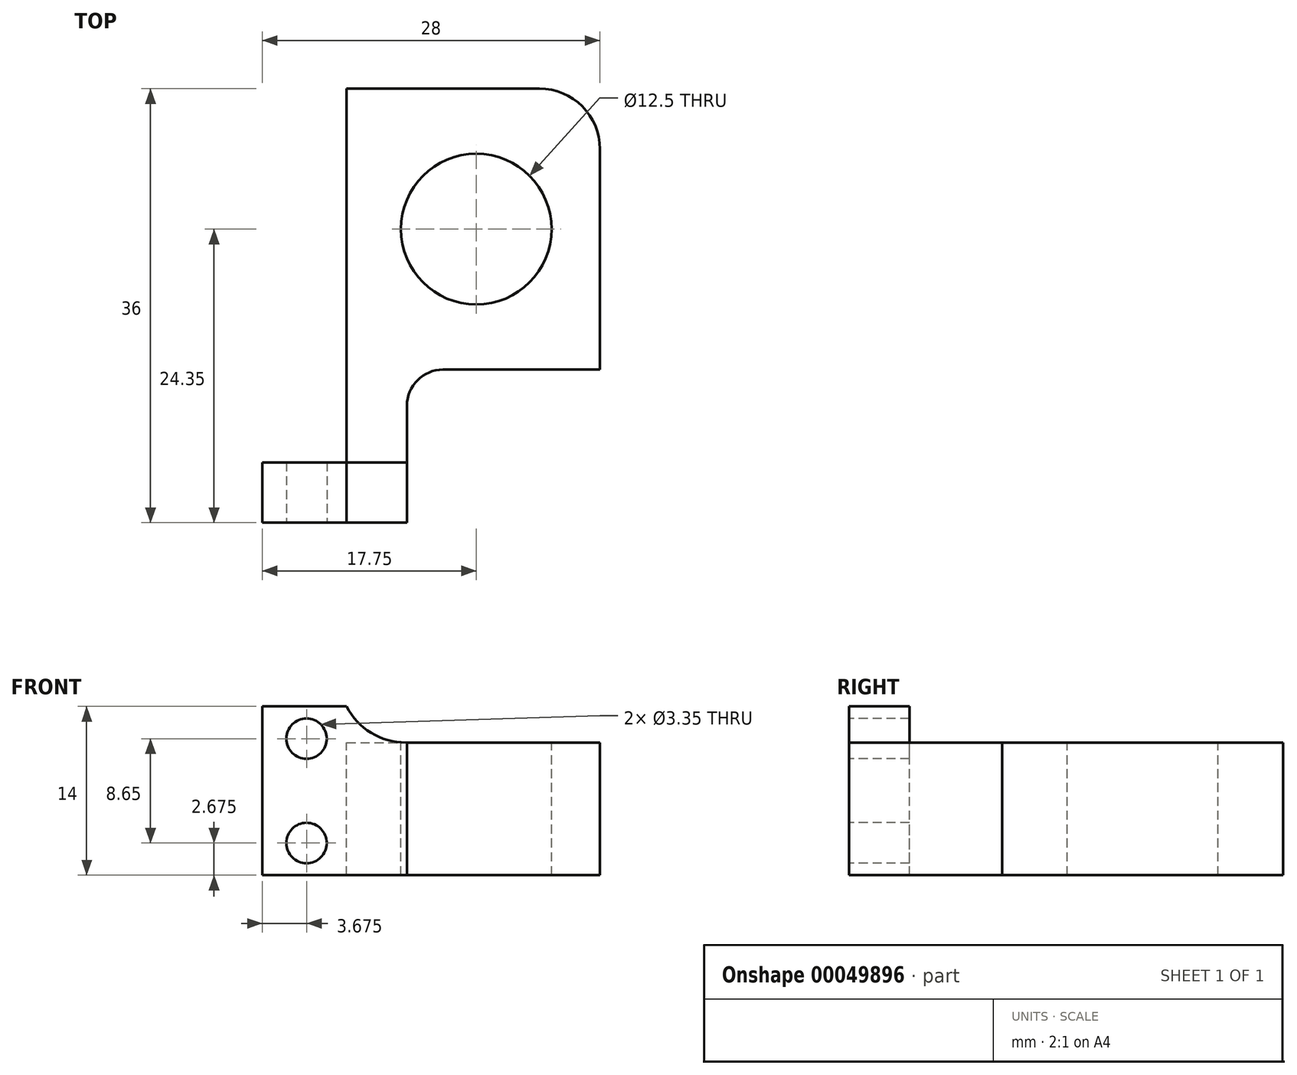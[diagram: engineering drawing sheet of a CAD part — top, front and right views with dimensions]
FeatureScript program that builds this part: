
annotation { "Feature Type Name" : "Feature", "Feature Type Description" : "" }
export const myFeature = defineFeature(function(context is Context, id is Id, definition is map)
    precondition{}
    {
        {
            var Q0;
            Q0=qCreatedBy(makeId("Top.planeOp"),FACE);
            var sketch = newSketch(context, id + "F0", { "sketchPlane" : qUnion([Q0])});
            skLineSegment(sketch, "E0.bottom", {"start": v(0, 0) * mm, "end": v(28, 0) * mm});
            skLineSegment(sketch, "E0.top", {"start": v(0, 36) * mm, "end": v(28, 36) * mm});
            skLineSegment(sketch, "E0.left", {"start": v(0, 0) * mm, "end": v(0, 36) * mm});
            skLineSegment(sketch, "E0.right", {"start": v(28, 0) * mm, "end": v(28, 36) * mm});
            skSolve(sketch);
        }
        {
            var Q0;
            Q0=qSketchRegion(id+"F0",true);
            extrude(context, id + "F1", {"entities" : qUnion([Q0]), "depth" : 4 * mm});
        }
        {
            var Q0;
            Q0=makeQuery(id+"F1.opExtrude","CAP_FACE",FACE,{"disambiguationData":[OSD([sQuery(id+"F0.wireOp",EDGE,"E0.bottom"),sQuery(id+"F0.wireOp",EDGE,"E0.top"),sQuery(id+"F0.wireOp",EDGE,"E0.left"),sQuery(id+"F0.wireOp",EDGE,"E0.right")])],"isStart":false});
            var sketch = newSketch(context, id + "F2", { "sketchPlane" : qUnion([Q0])});
            skCircle(sketch, "E1", {"center": v(17.75, 24.35) * mm, "radius": 6.25 * mm});
            skLineSegment(sketch, "E2.bottom", {"start": v(0, 36) * mm, "end": v(7, 36) * mm});
            skLineSegment(sketch, "E2.top", {"start": v(0, 5) * mm, "end": v(7, 5) * mm});
            skLineSegment(sketch, "E2.left", {"start": v(0, 36) * mm, "end": v(0, 5) * mm});
            skLineSegment(sketch, "E2.right", {"start": v(7, 36) * mm, "end": v(7, 5) * mm});
            skLineSegment(sketch, "E3.bottom", {"start": v(28, 0) * mm, "end": v(12, 0) * mm});
            skLineSegment(sketch, "E3.top", {"start": v(28, 12.7) * mm, "end": v(12, 12.7) * mm});
            skLineSegment(sketch, "E3.left", {"start": v(28, 0) * mm, "end": v(28, 12.7) * mm});
            skLineSegment(sketch, "E3.right", {"start": v(12, 0) * mm, "end": v(12, 12.7) * mm});
            skSolve(sketch);
        }
        {
            var Q0;
            Q0=qSketchRegion(id+"F2",true);
            extrude(context, id + "F3", {"entities" : qUnion([Q0]), "operationType" : NewBodyOperationType.REMOVE, "oppositeDirection" : true, "depth" : 25 * mm});
        }
        {
            var Q0;
            Q0=makeQuery(id+"F1.opExtrude","CAP_FACE",FACE,{"disambiguationData":[OSD([sQuery(id+"F0.wireOp",EDGE,"E0.bottom"),sQuery(id+"F0.wireOp",EDGE,"E0.top"),sQuery(id+"F0.wireOp",EDGE,"E0.left"),sQuery(id+"F0.wireOp",EDGE,"E0.right")])],"isStart":false});
            var sketch = newSketch(context, id + "F4", { "sketchPlane" : qUnion([Q0])});
            skLineSegment(sketch, "E4.bottom", {"start": v(0, 5) * mm, "end": v(7, 5) * mm});
            skLineSegment(sketch, "E4.top", {"start": v(0, 0) * mm, "end": v(7, 0) * mm});
            skLineSegment(sketch, "E4.left", {"start": v(0, 5) * mm, "end": v(0, 0) * mm});
            skLineSegment(sketch, "E4.right", {"start": v(7, 5) * mm, "end": v(7, 0) * mm});
            skSolve(sketch);
        }
        {
            var Q0;
            Q0=qSketchRegion(id+"F4",true);
            var Q1;
            {var subQ1=sQuery(id+"F4.wireOp",EDGE,"E4.right");Q1=makeQuery(id+"F4.imprint","IMPRINT",FACE,{"disambiguationData":[TD([[makeQuery(id+"F4.imprint","IMPRINT",EDGE,{"derivedFrom":subQ1}),1.0]])]});}
            extrude(context, id + "F5", {"entities" : qUnion([Q0, Q1]), "operationType" : NewBodyOperationType.ADD, "depth" : 7 * mm});
        }
        {
            var Q0;
            Q0=makeQuery(id+"F4.imprint","IMPRINT",FACE,{"disambiguationData":[TD([[makeQuery(id+"F4.imprint","IMPRINT",EDGE,{"derivedFrom":sQuery(id+"F4.wireOp",EDGE,"E4.bottom")}),-1.0]])]});
            extrude(context, id + "F6", {"entities" : qUnion([Q0]), "operationType" : NewBodyOperationType.ADD, "depth" : 10 * mm});
        }
        {
            var Q0;
            Q0=makeQuery(id+"F5.boolean.opBoolean","MERGE",FACE,{"derivedFrom":[makeQuery(id+"F1.opExtrude","SWEPT_FACE",FACE,{"disambiguationData":[OSD([sQuery(id+"F0.wireOp",EDGE,"E0.bottom")])]}),makeQuery(id+"F5.opExtrude","SWEPT_FACE",FACE,{"disambiguationData":[OSD([sQuery(id+"F4.wireOp",EDGE,"E4.top")])]})]});
            var sketch = newSketch(context, id + "F7", { "sketchPlane" : qUnion([Q0])});
            skCircle(sketch, "E5", {"center": v(3.68, 11.32) * mm, "radius": 1.67 * mm});
            skCircle(sketch, "E6", {"center": v(3.68, 2.68) * mm, "radius": 1.68 * mm});
            skLineSegment(sketch, "E7", {"start": v(3.68, 13) * mm, "end": v(3.68, 14) * mm});
            skLineSegment(sketch, "E8", {"start": v(3.68, 1) * mm, "end": v(3.68, 0) * mm});
            skSolve(sketch);
        }
        {
            var Q0;
            Q0=qSketchRegion(id+"F7",true);
            extrude(context, id + "F8", {"entities" : qUnion([Q0]), "operationType" : NewBodyOperationType.REMOVE, "oppositeDirection" : true, "depth" : 25 * mm});
        }
        {
            var Q0;
            Q0=makeQuery(id+"F1.opExtrude","SWEPT_EDGE",EDGE,{"disambiguationData":[OSD([sQuery(id+"F0.wireOp",EDGE,"E0.bottom"),sQuery(id+"F0.wireOp",EDGE,"E0.right")])]});
            var Q1;
            Q1=makeQuery(id+"F1.opExtrude","SWEPT_EDGE",EDGE,{"disambiguationData":[OSD([sQuery(id+"F0.wireOp",EDGE,"E0.top"),sQuery(id+"F0.wireOp",EDGE,"E0.right")])]});
            var Q2;
            Q2=makeQuery(id+"F3.boolean.opBoolean","COPY",EDGE,{"derivedFrom":makeQuery(id+"F3.opExtrude","SWEPT_EDGE",EDGE,{"disambiguationData":[OSD([sQuery(id+"F0.wireOp",EDGE,"E0.top"),sQuery(id+"F2.wireOp",EDGE,"E2.bottom"),sQuery(id+"F2.wireOp",EDGE,"E2.right")])]})});
            var Q3;
            Q3=makeQuery(id+"F3.boolean.opBoolean","COPY",EDGE,{"derivedFrom":makeQuery(id+"F3.opExtrude","SWEPT_EDGE",EDGE,{"disambiguationData":[OSD([sQuery(id+"F0.wireOp",EDGE,"E0.right"),sQuery(id+"F2.wireOp",EDGE,"E3.top"),sQuery(id+"F2.wireOp",EDGE,"E3.left")])]})});
            fillet(context, id + "F9", {"entities" : qUnion([Q0, Q1, Q2, Q3]), "radius" : 5 * mm, "tangentPropagation" : true, "allowEdgeOverflow" : false});
        }
        {
            var Q0;
            {var subQ0=sQuery(id+"F2.wireOp",EDGE,"E3.top");var subQ1=sQuery(id+"F2.wireOp",EDGE,"E3.right");Q0=makeQuery(id+"F5.boolean.opBoolean","MERGE",EDGE,{"derivedFrom":[makeQuery(id+"F3.boolean.opBoolean","COPY",EDGE,{"derivedFrom":makeQuery(id+"F3.opExtrude","SWEPT_EDGE",EDGE,{"disambiguationData":[OSD([subQ0,subQ1])]})}),makeQuery(id+"F5.opExtrude","SWEPT_EDGE",EDGE,{"disambiguationData":[OSD([subQ0,subQ1])]})]});}
            fillet(context, id + "F10", {"entities" : qUnion([Q0]), "radius" : 3 * mm, "tangentPropagation" : true, "allowEdgeOverflow" : false});
        }
        {
            var Q0;
            Q0=makeQuery(id+"F6.boolean.opBoolean","INTERSECT",EDGE,{"derivedFrom":[makeQuery(id+"F5.opExtrude","CAP_FACE",FACE,{"disambiguationData":[OSD([sQuery(id+"F0.wireOp",EDGE,"E0.bottom"),sQuery(id+"F0.wireOp",EDGE,"E0.top"),sQuery(id+"F0.wireOp",EDGE,"E0.right"),sQuery(id+"F2.wireOp",EDGE,"E1"),sQuery(id+"F2.wireOp",EDGE,"E2.right"),sQuery(id+"F2.wireOp",EDGE,"E3.top"),sQuery(id+"F2.wireOp",EDGE,"E3.right"),sQuery(id+"F4.wireOp",EDGE,"E4.bottom"),sQuery(id+"F4.wireOp",EDGE,"E4.top"),sQuery(id+"F4.wireOp",EDGE,"E4.left")])],"isStart":false}),makeQuery(id+"F6.opExtrude","SWEPT_FACE",FACE,{"disambiguationData":[OSD([sQuery(id+"F4.wireOp",EDGE,"E4.right")])]})]});
            fillet(context, id + "F11", {"entities" : qUnion([Q0]), "radius" : 5.5 * mm, "tangentPropagation" : true, "allowEdgeOverflow" : false});
        }
    });
